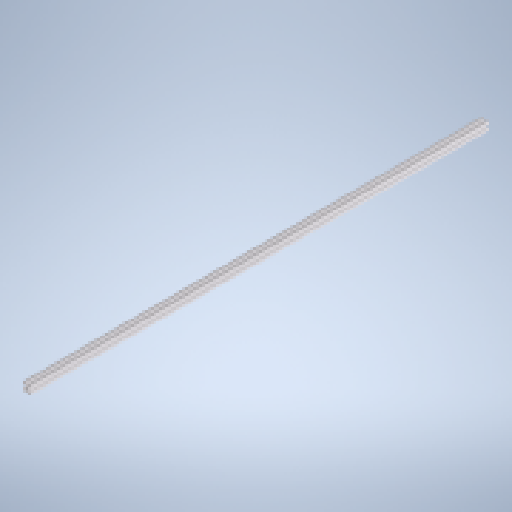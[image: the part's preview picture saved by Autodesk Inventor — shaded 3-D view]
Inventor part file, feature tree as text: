
AUTODESK INVENTOR PART (.ipt)
format: ipt  version: 2025 (Build 290162010, 162A)  size: 241,152 bytes
history: native  units: mm
features: thread x2, chamfer x2, other x1
ambient origin geometry x8: Origin, YZ Plane, XZ Plane, XY Plane, X Axis, Y Axis, Z Axis, Center Point
bodies: Volumenkörper1 (feature_tree)
feature tree (5):
  thread  "Gewinde1"  [1 undecoded]
  thread  "Gewinde2"  [1 undecoded]
  chamfer  "Fasen1"  Distance=2.0mm Angle=45.0deg
  chamfer  "Fasen2"  Distance=2.0mm Angle=45.0deg
  other  "item_43774_profil-5-20x20-1n-natur-_1096_high_1_1:1"
note: 2 required parameter values undecoded (feature->parameter linkage not recoverable at this tier; creation-order binding heuristic only, values carry confidence <= 0.55)
